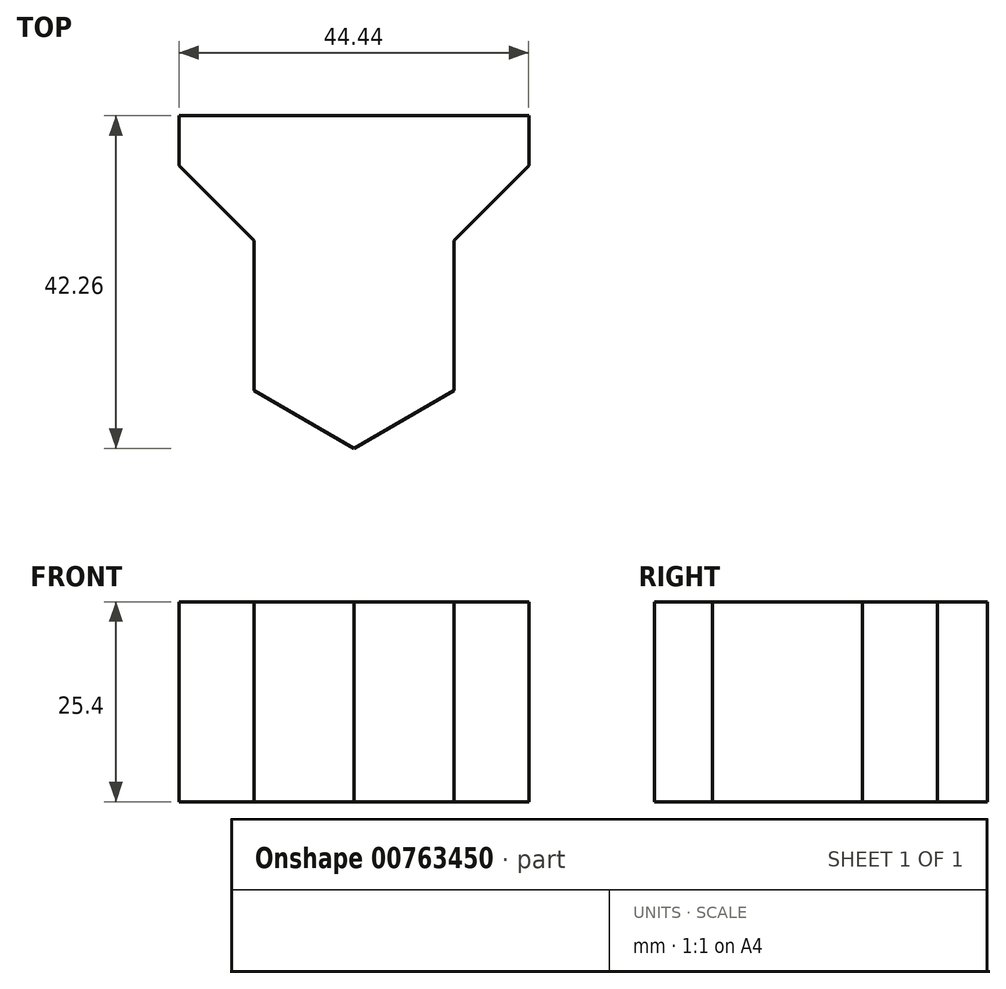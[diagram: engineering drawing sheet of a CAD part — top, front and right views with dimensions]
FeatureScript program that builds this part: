
annotation { "Feature Type Name" : "Feature", "Feature Type Description" : "" }
export const myFeature = defineFeature(function(context is Context, id is Id, definition is map)
    precondition{}
    {
        {
            var Q0;
            Q0=qCreatedBy(makeId("Top.planeOp"),FACE);
            var sketch = newSketch(context, id + "F0", { "sketchPlane" : qUnion([Q0])});
            skLineSegment(sketch, "E0", {"start": v(130.18, 0) * mm, "end": v(187.32, 0) * mm});
            skLineSegment(sketch, "E1", {"start": v(0, 22.07) * mm, "end": v(0, -42.52) * mm, "construction": true});
            skLineSegment(sketch, "E2", {"start": v(-12.7, 0) * mm, "end": v(-12.7, -25.4) * mm});
            skLineSegment(sketch, "E3", {"start": v(-12.7, -25.4) * mm, "end": v(0, -32.73) * mm});
            skLineSegment(sketch, "E4", {"start": v(0, -32.73) * mm, "end": v(12.7, -25.4) * mm});
            skLineSegment(sketch, "E5", {"start": v(12.7, -25.4) * mm, "end": v(12.7, 0) * mm});
            skLineSegment(sketch, "E6.trimOffspring", {"start": v(12.7, 0) * mm, "end": v(53.98, 0) * mm});
            skLineSegment(sketch, "E7", {"start": v(-152.4, 25.03) * mm, "end": v(-152.4, -43.75) * mm, "construction": true});
            skLineSegment(sketch, "E8", {"start": v(76.2, 20.98) * mm, "end": v(76.2, -40.03) * mm, "construction": true});
            skLineSegment(sketch, "E9", {"start": v(-177.8, 0) * mm, "end": v(-177.8, -12.7) * mm});
            skLineSegment(sketch, "E10", {"start": v(-177.8, -12.7) * mm, "end": v(-165.1, -12.7) * mm});
            skLineSegment(sketch, "E11", {"start": v(-165.1, -12.7) * mm, "end": v(-165.1, -28.58) * mm});
            skLineSegment(sketch, "E12", {"start": v(-165.1, -28.58) * mm, "end": v(-152.4, -35.9) * mm});
            skLineSegment(sketch, "E13", {"start": v(-152.4, -35.9) * mm, "end": v(-139.7, -28.58) * mm});
            skLineSegment(sketch, "E14", {"start": v(-139.7, -28.58) * mm, "end": v(-139.7, -12.7) * mm});
            skLineSegment(sketch, "E15", {"start": v(-139.7, -12.7) * mm, "end": v(-127, -12.7) * mm});
            skLineSegment(sketch, "E16", {"start": v(-127, -12.7) * mm, "end": v(-127, 0) * mm});
            skLineSegment(sketch, "E17.trimOffspring", {"start": v(-127, 0) * mm, "end": v(-12.7, 0) * mm});
            skLineSegment(sketch, "E18", {"start": v(53.98, 0) * mm, "end": v(63.5, -9.52) * mm});
            skLineSegment(sketch, "E19", {"start": v(63.5, -9.53) * mm, "end": v(63.5, -28.58) * mm});
            skLineSegment(sketch, "E20", {"start": v(63.5, -28.58) * mm, "end": v(76.2, -35.9) * mm});
            skLineSegment(sketch, "E21", {"start": v(76.2, -35.9) * mm, "end": v(88.9, -28.57) * mm});
            skLineSegment(sketch, "E22", {"start": v(88.9, -28.58) * mm, "end": v(88.9, -9.53) * mm});
            skLineSegment(sketch, "E23", {"start": v(88.9, -9.53) * mm, "end": v(98.43, 0) * mm});
            skLineSegment(sketch, "E24", {"start": v(63.5, -9.52) * mm, "end": v(76.2, -22.22) * mm, "construction": true});
            skLineSegment(sketch, "E25", {"start": v(76.2, -22.22) * mm, "end": v(88.9, -9.53) * mm, "construction": true});
            skLineSegment(sketch, "E26.trimOffspring", {"start": v(-88.9, 0) * mm, "end": v(98.43, 0) * mm});
            skLineSegment(sketch, "E27", {"start": v(-76.2, 33.52) * mm, "end": v(-76.2, -31.07) * mm, "construction": true});
            skLineSegment(sketch, "E28", {"start": v(-88.9, 0) * mm, "end": v(-88.9, -25.4) * mm});
            skLineSegment(sketch, "E29", {"start": v(-88.9, -25.4) * mm, "end": v(-76.2, -25.4) * mm});
            skLineSegment(sketch, "E30", {"start": v(-76.2, -25.4) * mm, "end": v(-63.5, -25.4) * mm});
            skLineSegment(sketch, "E31", {"start": v(-63.5, -25.4) * mm, "end": v(-63.5, 0) * mm});
            skLineSegment(sketch, "E32.trimOffspring", {"start": v(-190.5, 0) * mm, "end": v(-63.5, 0) * mm});
            skLineSegment(sketch, "E33", {"start": v(152.4, 14.58) * mm, "end": v(152.4, -46.43) * mm, "construction": true});
            skLineSegment(sketch, "E34", {"start": v(130.18, -6.35) * mm, "end": v(139.7, -15.88) * mm});
            skLineSegment(sketch, "E35", {"start": v(139.7, -15.88) * mm, "end": v(139.7, -34.92) * mm});
            skLineSegment(sketch, "E36", {"start": v(139.7, -34.92) * mm, "end": v(152.4, -42.26) * mm});
            skLineSegment(sketch, "E37", {"start": v(152.4, -42.26) * mm, "end": v(165.1, -34.93) * mm});
            skLineSegment(sketch, "E38", {"start": v(165.1, -34.92) * mm, "end": v(165.1, -15.88) * mm});
            skLineSegment(sketch, "E39", {"start": v(165.1, -15.88) * mm, "end": v(174.62, -6.35) * mm});
            skLineSegment(sketch, "E40", {"start": v(139.7, -15.88) * mm, "end": v(152.4, -28.58) * mm, "construction": true});
            skLineSegment(sketch, "E41", {"start": v(152.4, -28.57) * mm, "end": v(165.1, -15.88) * mm, "construction": true});
            skLineSegment(sketch, "E42", {"start": v(130.18, -6.35) * mm, "end": v(130.18, 0) * mm});
            skLineSegment(sketch, "E43", {"start": v(174.62, 0) * mm, "end": v(174.62, -6.35) * mm});
            skLineSegment(sketch, "E44.trimOffspring", {"start": v(-177.8, 0) * mm, "end": v(174.62, 0) * mm});
            skLineSegment(sketch, "E45", {"start": v(187.32, 0) * mm, "end": v(187.32, -50.8) * mm});
            skLineSegment(sketch, "E46", {"start": v(-190.5, -50.8) * mm, "end": v(187.32, -50.8) * mm});
            skLineSegment(sketch, "E47", {"start": v(-190.5, -50.8) * mm, "end": v(-190.5, 0) * mm});
            skSolve(sketch);
        }
        {
            var Q0;
            Q0=makeQuery(id+"F0.imprint","IMPRINT",FACE,{"disambiguationData":[TD([[makeQuery(id+"F0.imprint","IMPRINT",EDGE,{"derivedFrom":sQuery(id+"F0.wireOp",EDGE,"E0")}),-1.0]])]});
            extrude(context, id + "F1", {"entities" : qUnion([Q0]), "depth" : 25.4 * mm, "offsetDistance" : 25.4 * mm});
        }
    });
